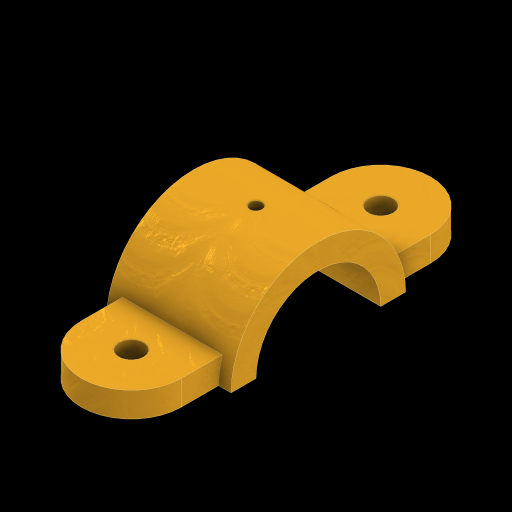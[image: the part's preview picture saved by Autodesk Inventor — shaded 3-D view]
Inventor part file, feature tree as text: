
AUTODESK INVENTOR PART (.ipt)
format: ipt  version: 2024 (Build 280153000, 153)  size: 219,136 bytes
history: native  units: in
note: dims shown in document units (in); Inventor stores cm internally (conversion verified against a paired STEP export)
features: extrude x6, sketch x5
ambient origin geometry x8: Origin, YZ Plane, XZ Plane, XY Plane, X Axis, Y Axis, Z Axis, Center Point
bodies: Solid1 (feature_tree)
feature tree (11):
  extrude  "BASE"  Depth=0.5in
  sketch  "Sketch2"  dims[d2=0.5in d3=1.0in]
  extrude  "REMOVED CENTER OF BASE"  Depth=1.0in
  extrude  "ARCH"  Depth=1.75in
  extrude  "TOPHOLE"  TaperAngle=0.0deg  [1 undecoded]
  extrude  "CIRCULAR"  Depth=1.25in
  extrude  "SQUARE"  TaperAngle=0.0deg  [1 undecoded]
  sketch  "Sketch1"  dims[d0=5.0in d1=0.5in]
  sketch  "Sketch3"  dims[d5=0.5in d6=0.0in d7=1.75in]
  sketch  "Sketch5"  dims[d8=1.25in d9=0.0in d10=0.0in]
  sketch  "Sketch6"  dims[d11=2.5in d12=0.0in d13=0.25in d14=0.0in d15=0.0in d16=2.5in d17=1.25in d18=0.625in d19=0.0in d20=0.0in d21=2.5in d22=0.0in d23=2.0in d24=1.0in d25=1.0in d26=1.25in]
note: 2 required parameter values undecoded (feature->parameter linkage not recoverable at this tier; creation-order binding heuristic only, values carry confidence <= 0.55)
